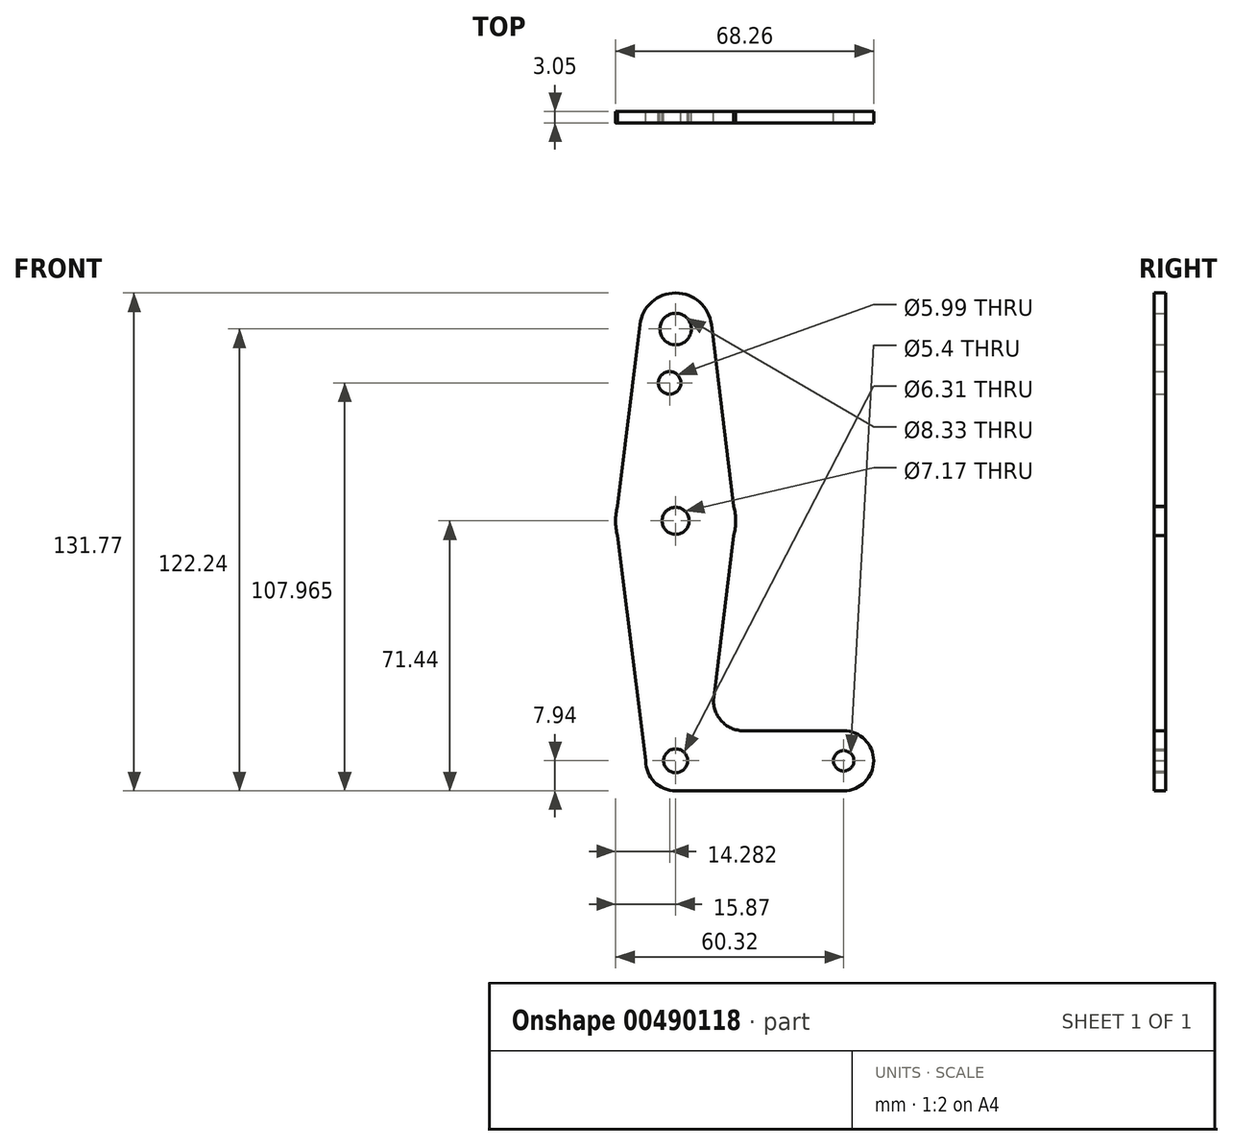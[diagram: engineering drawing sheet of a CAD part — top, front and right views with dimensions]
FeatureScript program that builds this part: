
annotation { "Feature Type Name" : "Feature", "Feature Type Description" : "" }
export const myFeature = defineFeature(function(context is Context, id is Id, definition is map)
    precondition{}
    {
        {
            var Q0;
            Q0=qCreatedBy(makeId("Front.planeOp"),FACE);
            var sketch = newSketch(context, id + "F0", { "sketchPlane" : qUnion([Q0])});
            skLineSegment(sketch, "E0", {"start": v(0, 0) * mm, "end": v(0, 114.3) * mm, "construction": true});
            skLineSegment(sketch, "E1", {"start": v(0, 0) * mm, "end": v(44.45, 0) * mm, "construction": true});
            skCircle(sketch, "E2", {"center": v(0, 114.3) * mm, "radius": 9.53 * mm});
            skCircle(sketch, "E3", {"center": v(0, 63.5) * mm, "radius": 15.88 * mm});
            skCircle(sketch, "E4", {"center": v(0, 0) * mm, "radius": 7.94 * mm});
            skCircle(sketch, "E5", {"center": v(44.45, 0) * mm, "radius": 7.94 * mm});
            skLineSegment(sketch, "E6", {"start": v(-15.88, 63.5) * mm, "end": v(-7.94, 0) * mm});
            skLineSegment(sketch, "E7", {"start": v(15.88, 63.5) * mm, "end": v(10.1, 16.87) * mm});
            skLineSegment(sketch, "E8", {"start": v(0, -7.94) * mm, "end": v(44.45, -7.94) * mm});
            skLineSegment(sketch, "E9", {"start": v(17.98, 7.94) * mm, "end": v(44.45, 7.94) * mm});
            skCircle(sketch, "E10", {"center": v(0, 0) * mm, "radius": 3.16 * mm});
            skCircle(sketch, "E11", {"center": v(44.45, 0) * mm, "radius": 2.7 * mm});
            skCircle(sketch, "E12", {"center": v(0, 114.3) * mm, "radius": 4.17 * mm});
            skCircle(sketch, "E13", {"center": v(0, 63.5) * mm, "radius": 3.59 * mm});
            skLineSegment(sketch, "E14", {"start": v(-15.4, 67.36) * mm, "end": v(-9.45, 115.47) * mm});
            skLineSegment(sketch, "E15", {"start": v(9.45, 115.47) * mm, "end": v(15.4, 67.36) * mm});
            skArc(sketch, "E16.filletArc", {"start": v(10.1, 16.87) * mm, "mid": v(12.02, 10.62) * mm, "end": v(17.98, 7.94) * mm});
            skPoint(sketch, "E17.centerSnap0", {"position": v(-12.43, 91.42) * mm});
            skCircle(sketch, "E18", {"center": v(-1.59, 100.03) * mm, "radius": 3 * mm});
            skSolve(sketch);
        }
        {
            var Q0;
            Q0 = qSketchRegion(id + "F0", true);
            extrude(context, id + "F1", {"entities" : qUnion([Q0]), "depth" : 3.05 * mm});
        }
    });
